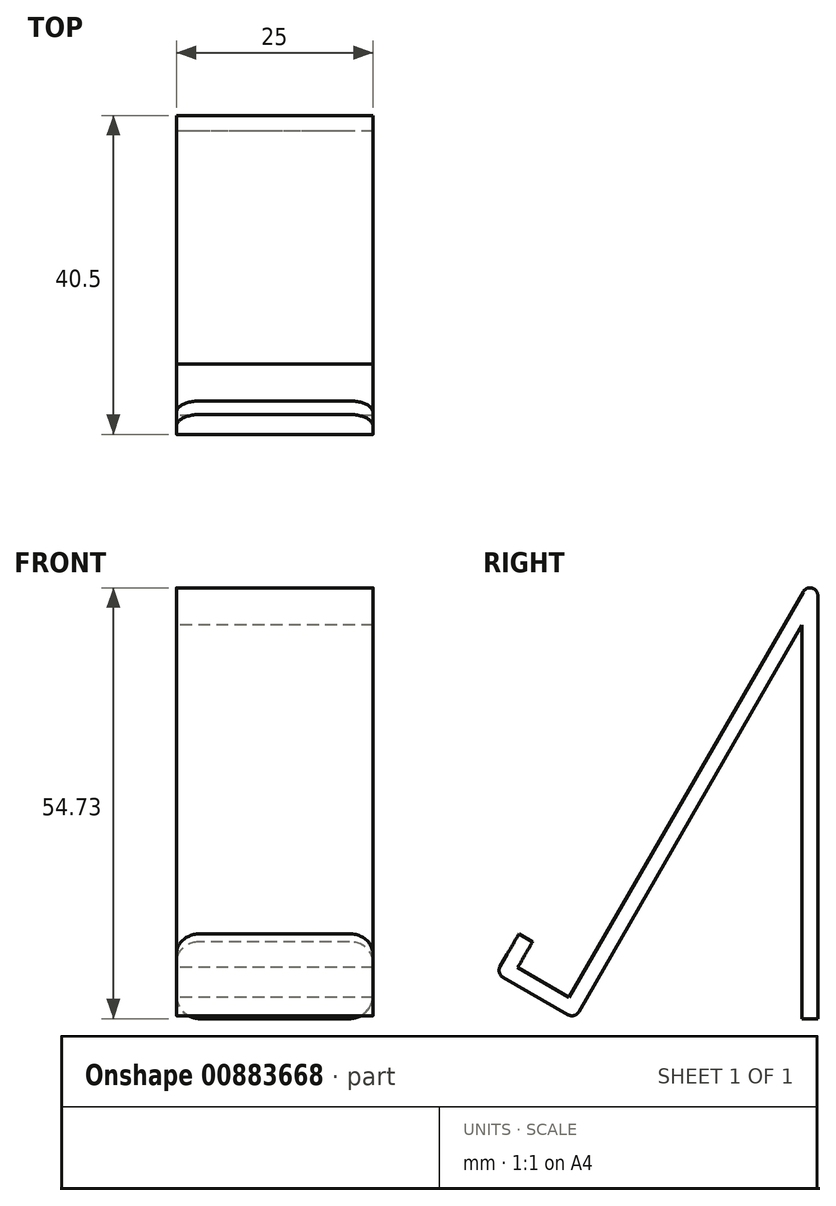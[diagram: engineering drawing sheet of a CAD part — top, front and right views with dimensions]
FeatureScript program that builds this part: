
annotation { "Feature Type Name" : "Feature", "Feature Type Description" : "" }
export const myFeature = defineFeature(function(context is Context, id is Id, definition is map)
    precondition{}
    {
        {
            var Q0;
            Q0=qCreatedBy(makeId("Right.planeOp"),FACE);
            var sketch = newSketch(context, id + "F0", { "sketchPlane" : qUnion([Q0])});
            skLineSegment(sketch, "E0", {"start": v(0, 25) * mm, "end": v(0, -25) * mm});
            skLineSegment(sketch, "E1", {"start": v(0, 25) * mm, "end": v(-28.87, -25) * mm});
            skLineSegment(sketch, "E2", {"start": v(-28.87, -25) * mm, "end": v(-38.87, -19.23) * mm});
            skLineSegment(sketch, "E3", {"start": v(-38.87, -19.23) * mm, "end": v(-35.98, -14.23) * mm});
            skLineSegment(sketch, "E4.0", {"start": v(-36.14, -18.5) * mm, "end": v(-34.25, -15.23) * mm});
            skLineSegment(sketch, "E4.1", {"start": v(-29.6, -22.27) * mm, "end": v(-36.14, -18.5) * mm});
            skLineSegment(sketch, "E4.2", {"start": v(2, 32.46) * mm, "end": v(-29.6, -22.27) * mm});
            skLineSegment(sketch, "E4.3", {"start": v(2, 32.46) * mm, "end": v(2, -25) * mm});
            skLineSegment(sketch, "E5", {"start": v(-35.98, -14.23) * mm, "end": v(-34.25, -15.23) * mm});
            skLineSegment(sketch, "E6", {"start": v(0, -25) * mm, "end": v(2, -25) * mm});
            skSolve(sketch);
        }
        {
            var Q0;
            Q0=makeQuery(id+"F0.imprint","IMPRINT",FACE,{"disambiguationData":[TD([[makeQuery(id+"F0.imprint","IMPRINT",EDGE,{"derivedFrom":sQuery(id+"F0.wireOp",EDGE,"E0")}),1.0]])]});
            extrude(context, id + "F1", {"entities" : qUnion([Q0]), "endBound" : BoundingType.SYMMETRIC, "depth" : 25 * mm, "offsetDistance" : 25 * mm});
        }
        {
            var Q0;
            Q0=makeQuery(id+"F1.opExtrude","SWEPT_EDGE",EDGE,{"disambiguationData":[OSD([sQuery(id+"F0.wireOp",EDGE,"E4.2"),sQuery(id+"F0.wireOp",EDGE,"E4.3")])]});
            var Q1;
            Q1=makeQuery(id+"F1.opExtrude","SWEPT_EDGE",EDGE,{"disambiguationData":[OSD([sQuery(id+"F0.wireOp",EDGE,"E2"),sQuery(id+"F0.wireOp",EDGE,"E3")])]});
            var Q2;
            Q2=makeQuery(id+"F1.opExtrude","SWEPT_EDGE",EDGE,{"disambiguationData":[OSD([sQuery(id+"F0.wireOp",EDGE,"E1"),sQuery(id+"F0.wireOp",EDGE,"E2")])]});
            fillet(context, id + "F2", {"entities" : qUnion([Q0, Q1, Q2]), "radius" : 1 * mm, "tangentPropagation" : true, "allowEdgeOverflow" : false});
        }
        {
            var Q0;
            Q0=makeQuery(id+"F1.opExtrude","CAP_EDGE",EDGE,{"disambiguationData":[OSD([sQuery(id+"F0.wireOp",EDGE,"E6")])],"isStart":false});
            var Q1;
            Q1=makeQuery(id+"F1.opExtrude","CAP_EDGE",EDGE,{"disambiguationData":[OSD([sQuery(id+"F0.wireOp",EDGE,"E6")])],"isStart":true});
            var Q2;
            Q2=makeQuery(id+"F1.opExtrude","CAP_EDGE",EDGE,{"disambiguationData":[OSD([sQuery(id+"F0.wireOp",EDGE,"E5")])],"isStart":false});
            var Q3;
            Q3=makeQuery(id+"F1.opExtrude","CAP_EDGE",EDGE,{"disambiguationData":[OSD([sQuery(id+"F0.wireOp",EDGE,"E5")])],"isStart":true});
            fillet(context, id + "F3", {"entities" : qUnion([Q0, Q1, Q2, Q3]), "radius" : 3 * mm, "tangentPropagation" : true, "allowEdgeOverflow" : false});
        }
    });
